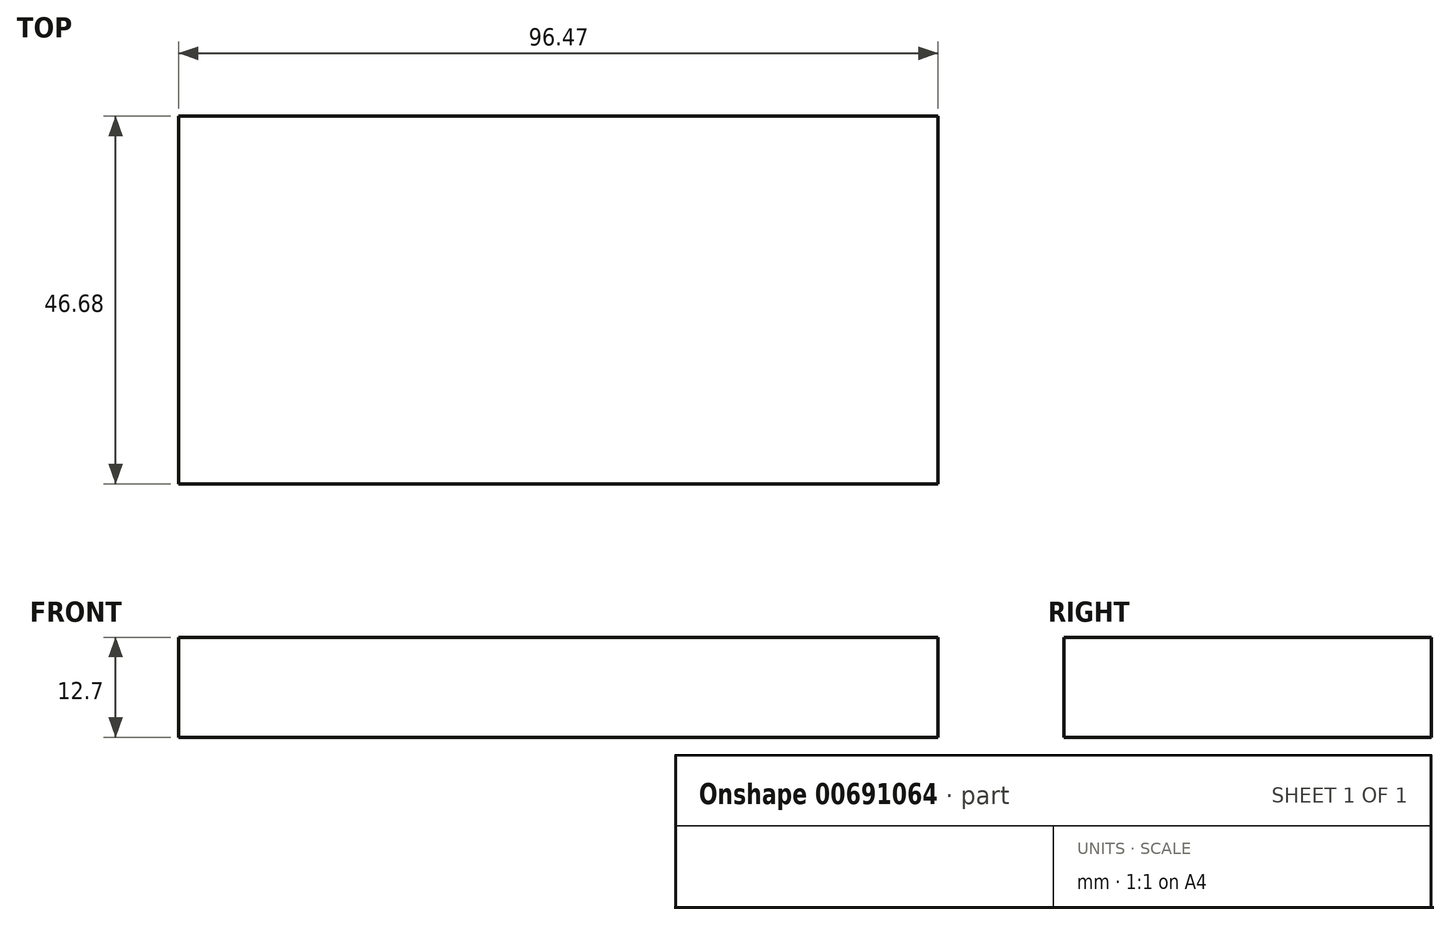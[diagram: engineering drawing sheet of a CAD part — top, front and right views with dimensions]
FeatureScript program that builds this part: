
annotation { "Feature Type Name" : "Feature", "Feature Type Description" : "" }
export const myFeature = defineFeature(function(context is Context, id is Id, definition is map)
    precondition{}
    {
        {
            var Q0;
            Q0=qCreatedBy(makeId("Top.planeOp"),FACE);
            var sketch = newSketch(context, id + "F0", { "sketchPlane" : qUnion([Q0])});
            skLineSegment(sketch, "E0.bottom", {"start": v(-51.45, 31.95) * mm, "end": v(45.02, 31.95) * mm});
            skLineSegment(sketch, "E0.top", {"start": v(-51.45, -14.73) * mm, "end": v(45.02, -14.73) * mm});
            skLineSegment(sketch, "E0.left", {"start": v(-51.45, 31.95) * mm, "end": v(-51.45, -14.73) * mm});
            skLineSegment(sketch, "E0.right", {"start": v(45.02, 31.95) * mm, "end": v(45.02, -14.73) * mm});
            skSolve(sketch);
        }
        {
            var Q0;
            Q0 = qSketchRegion(id + "F0", true);
            extrude(context, id + "F1", {"entities" : qUnion([Q0]), "depth" : 12.7 * mm, "offsetDistance" : 25.4 * mm});
        }
    });
